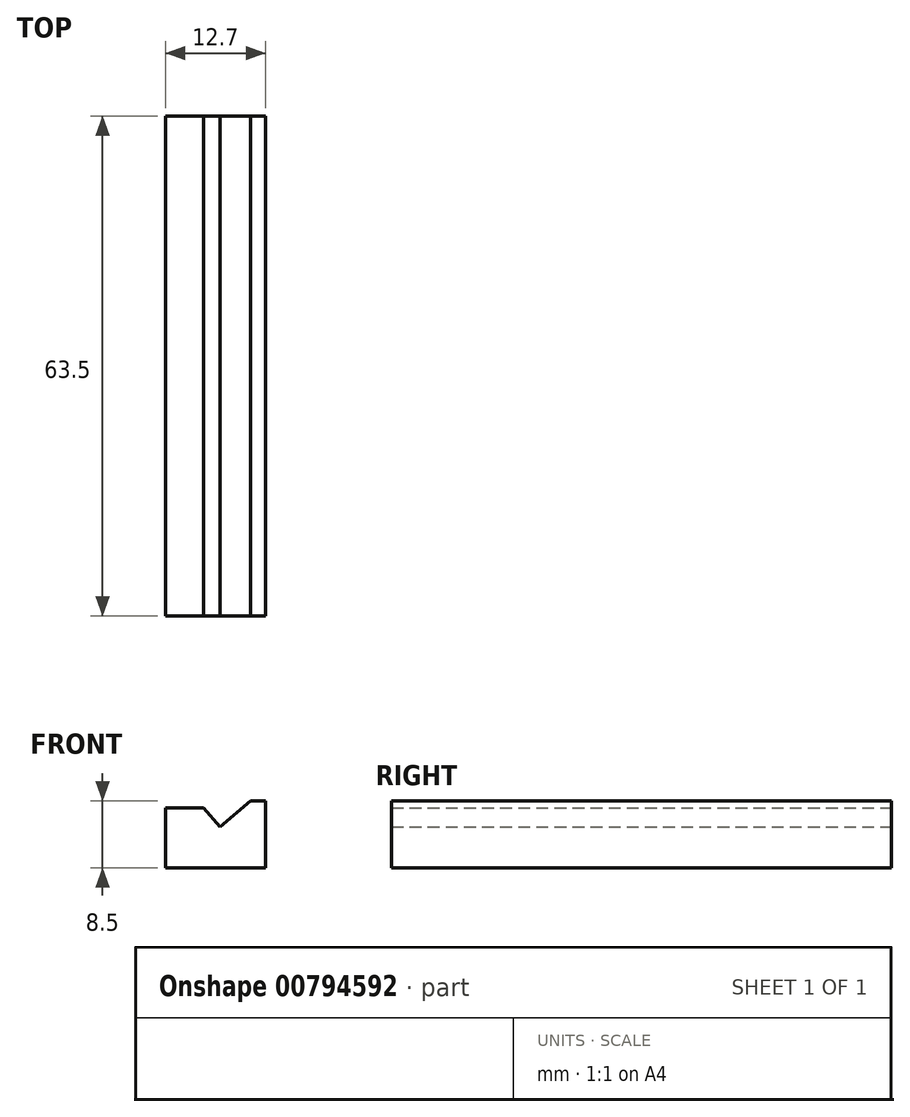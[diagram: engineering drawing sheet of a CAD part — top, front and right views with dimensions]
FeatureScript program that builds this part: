
annotation { "Feature Type Name" : "Feature", "Feature Type Description" : "" }
export const myFeature = defineFeature(function(context is Context, id is Id, definition is map)
    precondition{}
    {
        {
            var Q0;
            Q0=qCreatedBy(makeId("Front.planeOp"),FACE);
            var sketch = newSketch(context, id + "F0", { "sketchPlane" : qUnion([Q0])});
            skLineSegment(sketch, "E0", {"start": v(-4.82, 3.9) * mm, "end": v(-4.82, -3.72) * mm});
            skLineSegment(sketch, "E1", {"start": v(-4.82, -3.72) * mm, "end": v(7.88, -3.72) * mm});
            skLineSegment(sketch, "E2", {"start": v(2.12, 1.46) * mm, "end": v(0, 3.9) * mm});
            skLineSegment(sketch, "E3", {"start": v(0, 3.9) * mm, "end": v(-4.82, 3.9) * mm});
            skLineSegment(sketch, "E4", {"start": v(7.88, 4.78) * mm, "end": v(5.96, 4.78) * mm});
            skLineSegment(sketch, "E5", {"start": v(2.12, 1.46) * mm, "end": v(5.96, 4.78) * mm});
            skLineSegment(sketch, "E6", {"start": v(7.88, 4.78) * mm, "end": v(7.88, -3.72) * mm});
            skSolve(sketch);
        }
        {
            var Q0;
            Q0=makeQuery(id+"F0.imprint","IMPRINT",FACE,{"disambiguationData":[TD([[makeQuery(id+"F0.imprint","IMPRINT",EDGE,{"derivedFrom":sQuery(id+"F0.wireOp",EDGE,"E0")}),1.0]])]});
            extrude(context, id + "F1", {"entities" : qUnion([Q0]), "depth" : 63.5 * mm, "offsetDistance" : 25.4 * mm});
        }
    });
